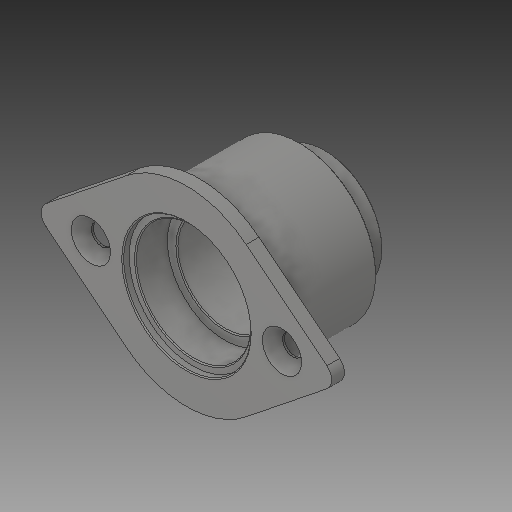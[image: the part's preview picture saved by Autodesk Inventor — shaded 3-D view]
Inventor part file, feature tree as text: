
AUTODESK INVENTOR PART (.ipt)
format: ipt  version: 2017 (Build 210142000, 142)  size: 179,712 bytes
history: native  units: in
note: dims shown in document units (in); Inventor stores cm internally (conversion verified against a paired STEP export)
features: chamfer x1
ambient origin geometry x8: Origin, YZ Plane, XZ Plane, XY Plane, X Axis, Y Axis, Z Axis, Center Point
bodies: Solid1 (feature_tree)
feature tree (1):
  chamfer  "Chamfer1"  [1 undecoded]
note: 1 required parameter value undecoded (feature->parameter linkage not recoverable at this tier; creation-order binding heuristic only, values carry confidence <= 0.55)
